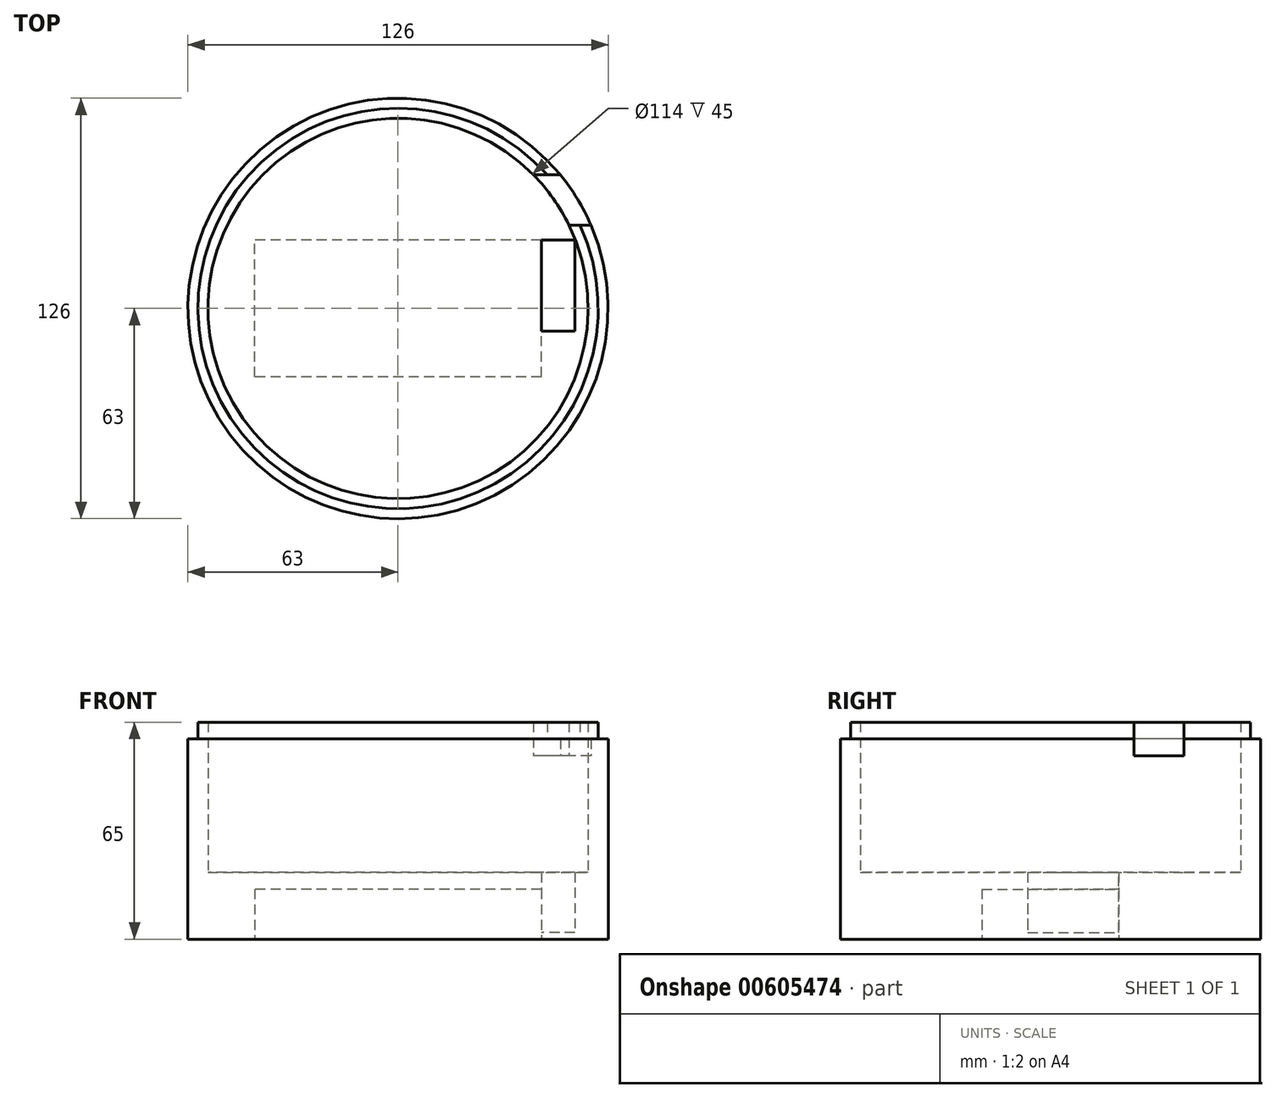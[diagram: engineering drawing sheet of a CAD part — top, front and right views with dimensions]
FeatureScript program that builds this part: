
annotation { "Feature Type Name" : "Feature", "Feature Type Description" : "" }
export const myFeature = defineFeature(function(context is Context, id is Id, definition is map)
    precondition{}
    {
        {
            var Q0;
            Q0=qCreatedBy(makeId("Top.planeOp"),FACE);
            var sketch = newSketch(context, id + "F0", { "sketchPlane" : qUnion([Q0])});
            skCircle(sketch, "E0", {"center": v(0, 0) * mm, "radius": 63 * mm});
            skCircle(sketch, "E1", {"center": v(0, 0) * mm, "radius": 60 * mm});
            skSolve(sketch);
        }
        {
            var Q0;
            Q0=qCreatedBy(makeId("Top.planeOp"),FACE);
            var sketch = newSketch(context, id + "F1", { "sketchPlane" : qUnion([Q0])});
            skCircle(sketch, "E2", {"center": v(0, 0) * mm, "radius": 57 * mm});
            skCircle(sketch, "E3", {"center": v(0, 0) * mm, "radius": 60 * mm});
            skSolve(sketch);
        }
        {
            var Q0;
            Q0=makeQuery(id+"F0.imprint","IMPRINT",FACE,{"disambiguationData":[TD([[makeQuery(id+"F0.imprint","IMPRINT",EDGE,{"derivedFrom":sQuery(id+"F0.wireOp",EDGE,"E0")}),1.0]])]});
            extrude(context, id + "F2", {"entities" : qUnion([Q0]), "depth" : 60 * mm, "offsetDistance" : 25 * mm});
        }
        {
            var Q0;
            Q0=qSketchRegion(id+"F1",true);
            extrude(context, id + "F3", {"entities" : qUnion([Q0]), "operationType" : NewBodyOperationType.ADD, "depth" : 65 * mm, "offsetDistance" : 25 * mm});
        }
        {
            var Q0;
            Q0=qCreatedBy(makeId("Top.planeOp"),FACE);
            var sketch = newSketch(context, id + "F4", { "sketchPlane" : qUnion([Q0])});
            skCircle(sketch, "E4", {"center": v(0, 0) * mm, "radius": 57 * mm});
            skSolve(sketch);
        }
        {
            var Q0;
            Q0=qSketchRegion(id+"F4",true);
            var Q1;
            Q1=qSketchRegion(id+"F7",true);
            extrude(context, id + "F5", {"entities" : qUnion([Q0, Q1]), "operationType" : NewBodyOperationType.ADD, "depth" : 60 * mm, "offsetDistance" : 25 * mm});
        }
        {
            var Q0;
            Q0=qCreatedBy(makeId("Top.planeOp"),FACE);
            cPlane(context, id + "F6", {"entities" : qUnion([Q0]), "cplaneType" : CPlaneType.OFFSET, "offset" : 45 * mm, "width" : 150 * mm, "height" : 150 * mm});
        }
        {
            var Q0;
            Q0=qCreatedBy(id+"F6.planeOp",FACE);
            var sketch = newSketch(context, id + "F7", { "sketchPlane" : qUnion([Q0])});
            skCircle(sketch, "E5", {"center": v(0, 0) * mm, "radius": 57 * mm});
            skSolve(sketch);
        }
        {
            var Q0;
            Q0=qSketchRegion(id+"F7",true);
            extrude(context, id + "F8", {"entities" : qUnion([Q0]), "operationType" : NewBodyOperationType.REMOVE, "oppositeDirection" : true, "depth" : 40 * mm, "offsetDistance" : 25 * mm});
        }
        {
            var Q0;
            Q0=qCreatedBy(makeId("Right.planeOp"),FACE);
            var sketch = newSketch(context, id + "F9", { "sketchPlane" : qUnion([Q0])});
            skLineSegment(sketch, "E6", {"start": v(0, 0) * mm, "end": v(25, 0) * mm, "construction": true});
            skLineSegment(sketch, "E7", {"start": v(25, 0) * mm, "end": v(25, 65) * mm, "construction": true});
            skLineSegment(sketch, "E8.bottom", {"start": v(25, 65) * mm, "end": v(40, 65) * mm});
            skLineSegment(sketch, "E8.top", {"start": v(25, 55) * mm, "end": v(40, 55) * mm});
            skLineSegment(sketch, "E8.left", {"start": v(25, 65) * mm, "end": v(25, 55) * mm});
            skLineSegment(sketch, "E8.right", {"start": v(40, 65) * mm, "end": v(40, 55) * mm});
            skSolve(sketch);
        }
        {
            var Q0;
            Q0=makeQuery(id+"F9.imprint","IMPRINT",FACE,{"disambiguationData":[TD([[makeQuery(id+"F9.imprint","IMPRINT",EDGE,{"derivedFrom":sQuery(id+"F9.wireOp",EDGE,"E8.bottom")}),-1.0]])]});
            extrude(context, id + "F10", {"entities" : qUnion([Q0]), "operationType" : NewBodyOperationType.REMOVE, "depth" : 279.5 * mm, "offsetDistance" : 25 * mm});
        }
        {
            var Q0;
            Q0=makeQuery(id+"F1.imprint","IMPRINT",FACE,{"disambiguationData":[TD([[makeQuery(id+"F1.imprint","IMPRINT",EDGE,{"derivedFrom":sQuery(id+"F1.wireOp",EDGE,"E2")}),1.0]])]});
            extrude(context, id + "F11", {"entities" : qUnion([Q0]), "operationType" : NewBodyOperationType.REMOVE, "depth" : 71.5 * mm, "offsetDistance" : 25 * mm});
        }
        {
            var Q0;
            Q0=qCreatedBy(makeId("Top.planeOp"),FACE);
            cPlane(context, id + "F12", {"entities" : qUnion([Q0]), "cplaneType" : CPlaneType.OFFSET, "offset" : 15 * mm, "width" : 150 * mm, "height" : 150 * mm});
        }
        {
            var Q0;
            Q0=qCreatedBy(makeId("Top.planeOp"),FACE);
            var sketch = newSketch(context, id + "F13", { "sketchPlane" : qUnion([Q0])});
            skCircle(sketch, "E9", {"center": v(0, 0) * mm, "radius": 63 * mm});
            skSolve(sketch);
        }
        {
            var Q0;
            Q0=qSketchRegion(id+"F13",true);
            extrude(context, id + "F14", {"entities" : qUnion([Q0]), "operationType" : NewBodyOperationType.ADD, "depth" : 20 * mm, "offsetDistance" : 25 * mm});
        }
        {
            var Q0;
            Q0=qCreatedBy(makeId("Top.planeOp"),FACE);
            var sketch = newSketch(context, id + "F15", { "sketchPlane" : qUnion([Q0])});
            skLineSegment(sketch, "E10.bottom", {"start": v(43, -20.5) * mm, "end": v(-43, -20.5) * mm});
            skLineSegment(sketch, "E10.top", {"start": v(43, 20.5) * mm, "end": v(-43, 20.5) * mm});
            skLineSegment(sketch, "E10.left", {"start": v(43, -20.5) * mm, "end": v(43, 20.5) * mm});
            skLineSegment(sketch, "E10.right", {"start": v(-43, -20.5) * mm, "end": v(-43, 20.5) * mm});
            skPoint(sketch, "E10.middle", {"position": v(0, 0) * mm});
            skSolve(sketch);
        }
        {
            var Q0;
            Q0=makeQuery(id+"F15.imprint","IMPRINT",FACE,{"disambiguationData":[TD([[makeQuery(id+"F15.imprint","IMPRINT",EDGE,{"derivedFrom":sQuery(id+"F15.wireOp",EDGE,"E10.bottom")}),-1.0]])]});
            var Q1;
            Q1 = qSketchRegion(id + "F17", true);
            extrude(context, id + "F16", {"entities" : qUnion([Q0, Q1]), "operationType" : NewBodyOperationType.REMOVE, "depth" : 15 * mm, "offsetDistance" : 25 * mm});
        }
        {
            var Q0;
            Q0=qCreatedBy(makeId("Right.planeOp"),FACE);
            var sketch = newSketch(context, id + "F17", { "sketchPlane" : qUnion([Q0])});
            skLineSegment(sketch, "E11", {"start": v(0, 0) * mm, "end": v(-6.83, 0) * mm, "construction": true});
            skLineSegment(sketch, "E12", {"start": v(-6.83, 0) * mm, "end": v(-6.83, 2) * mm, "construction": true});
            skLineSegment(sketch, "E13", {"start": v(-6.83, 2) * mm, "end": v(20.47, 2) * mm});
            skLineSegment(sketch, "E14", {"start": v(20.47, 2) * mm, "end": v(20.47, 15) * mm});
            skLineSegment(sketch, "E15", {"start": v(20.47, 15) * mm, "end": v(-6.83, 15) * mm});
            skLineSegment(sketch, "E16", {"start": v(-6.83, 15) * mm, "end": v(-6.83, 2) * mm});
            skSolve(sketch);
        }
        {
            var Q0;
            Q0 = qSketchRegion(id + "F17", true);
            extrude(context, id + "F18", {"entities" : qUnion([Q0]), "operationType" : NewBodyOperationType.REMOVE, "depth" : 53 * mm, "offsetDistance" : 25 * mm});
        }
        {
            var Q0;
            Q0=qCreatedBy(id+"F12.planeOp",FACE);
            var sketch = newSketch(context, id + "F19", { "sketchPlane" : qUnion([Q0])});
            skLineSegment(sketch, "E17", {"start": v(0, 0) * mm, "end": v(43, 0) * mm, "construction": true});
            skLineSegment(sketch, "E18", {"start": v(43, 0) * mm, "end": v(43, -6.83) * mm});
            skLineSegment(sketch, "E19", {"start": v(43, -6.83) * mm, "end": v(53, -6.83) * mm});
            skLineSegment(sketch, "E20", {"start": v(53, -6.83) * mm, "end": v(53, 20.47) * mm});
            skLineSegment(sketch, "E21", {"start": v(53, 20.47) * mm, "end": v(43, 20.47) * mm});
            skLineSegment(sketch, "E22", {"start": v(43, 20.47) * mm, "end": v(43, 0) * mm});
            skSolve(sketch);
        }
        {
            var Q0;
            Q0 = qSketchRegion(id + "F19", true);
            extrude(context, id + "F20", {"entities" : qUnion([Q0]), "operationType" : NewBodyOperationType.REMOVE, "depth" : 25 * mm, "offsetDistance" : 25 * mm});
        }
    });
